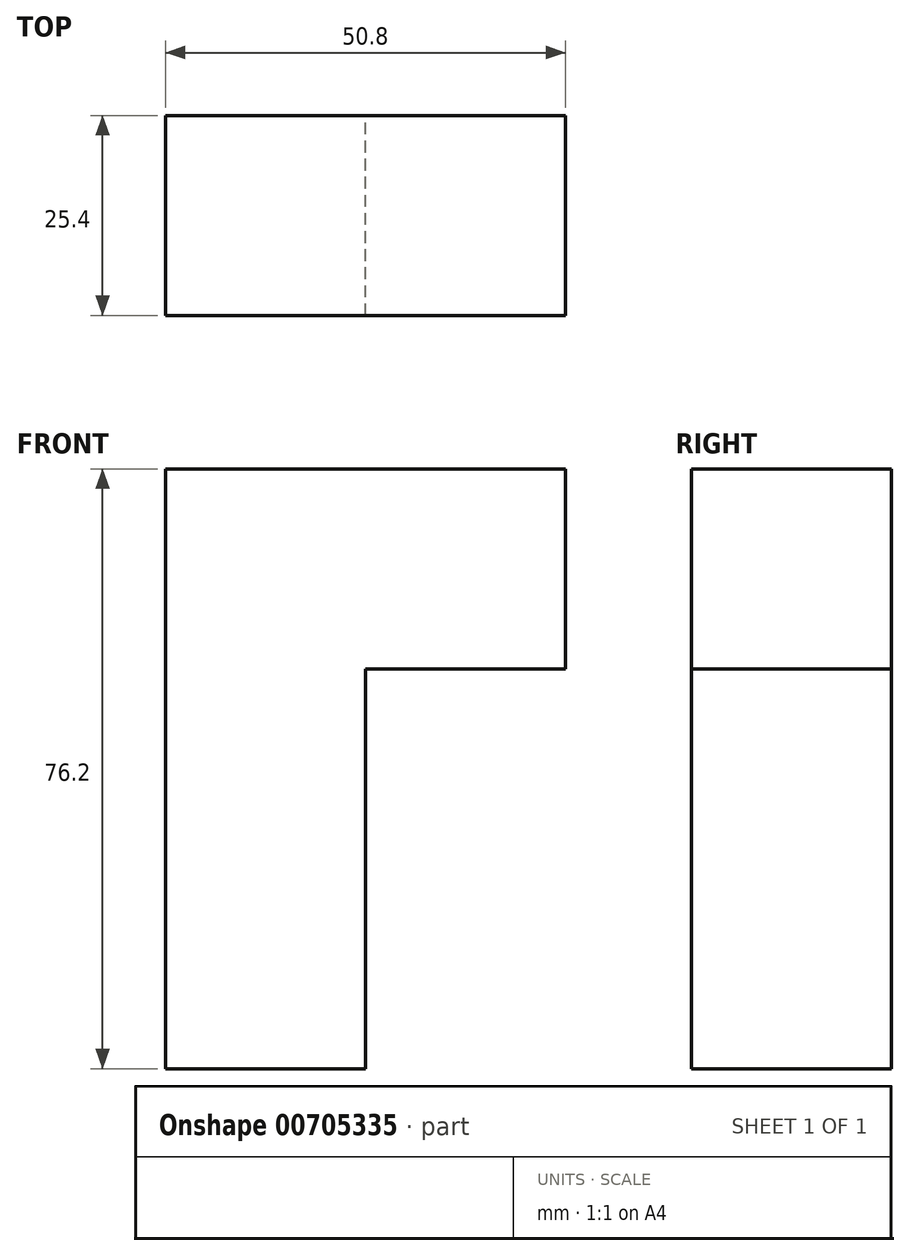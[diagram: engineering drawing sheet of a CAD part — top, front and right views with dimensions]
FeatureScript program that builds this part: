
annotation { "Feature Type Name" : "Feature", "Feature Type Description" : "" }
export const myFeature = defineFeature(function(context is Context, id is Id, definition is map)
    precondition{}
    {
        {
            var Q0;
            Q0=qCreatedBy(makeId("Front.planeOp"),FACE);
            var sketch = newSketch(context, id + "F0", { "sketchPlane" : qUnion([Q0])});
            skLineSegment(sketch, "E0.bottom", {"start": v(0, 25.4) * mm, "end": v(-25.4, 25.4) * mm});
            skLineSegment(sketch, "E0.top", {"start": v(0, 0) * mm, "end": v(-25.4, 0) * mm});
            skLineSegment(sketch, "E0.left", {"start": v(0, 25.4) * mm, "end": v(0, 0) * mm});
            skLineSegment(sketch, "E0.right", {"start": v(-25.4, 25.4) * mm, "end": v(-25.4, 0) * mm});
            skLineSegment(sketch, "E1.bottom", {"start": v(-25.4, 25.4) * mm, "end": v(0, 25.4) * mm});
            skLineSegment(sketch, "E1.top", {"start": v(-25.4, 50.8) * mm, "end": v(0, 50.8) * mm});
            skLineSegment(sketch, "E1.left", {"start": v(-25.4, 25.4) * mm, "end": v(-25.4, 50.8) * mm});
            skLineSegment(sketch, "E1.right", {"start": v(0, 25.4) * mm, "end": v(0, 50.8) * mm});
            skLineSegment(sketch, "E2.top", {"start": v(-25.4, 76.2) * mm, "end": v(0, 76.2) * mm});
            skLineSegment(sketch, "E2.left", {"start": v(-25.4, 50.8) * mm, "end": v(-25.4, 76.2) * mm});
            skLineSegment(sketch, "E2.right", {"start": v(0, 50.8) * mm, "end": v(0, 76.2) * mm});
            skLineSegment(sketch, "E3.bottom", {"start": v(0, 76.2) * mm, "end": v(25.4, 76.2) * mm});
            skLineSegment(sketch, "E3.top", {"start": v(0, 50.8) * mm, "end": v(25.4, 50.8) * mm});
            skLineSegment(sketch, "E3.left", {"start": v(0, 76.2) * mm, "end": v(0, 50.8) * mm});
            skLineSegment(sketch, "E3.right", {"start": v(25.4, 76.2) * mm, "end": v(25.4, 50.8) * mm});
            skSolve(sketch);
        }
        {
            var Q0;
            Q0 = qSketchRegion(id + "F0", true);
            extrude(context, id + "F1", {"entities" : qUnion([Q0]), "depth" : 25.4 * mm, "offsetDistance" : 25.4 * mm});
        }
    });
